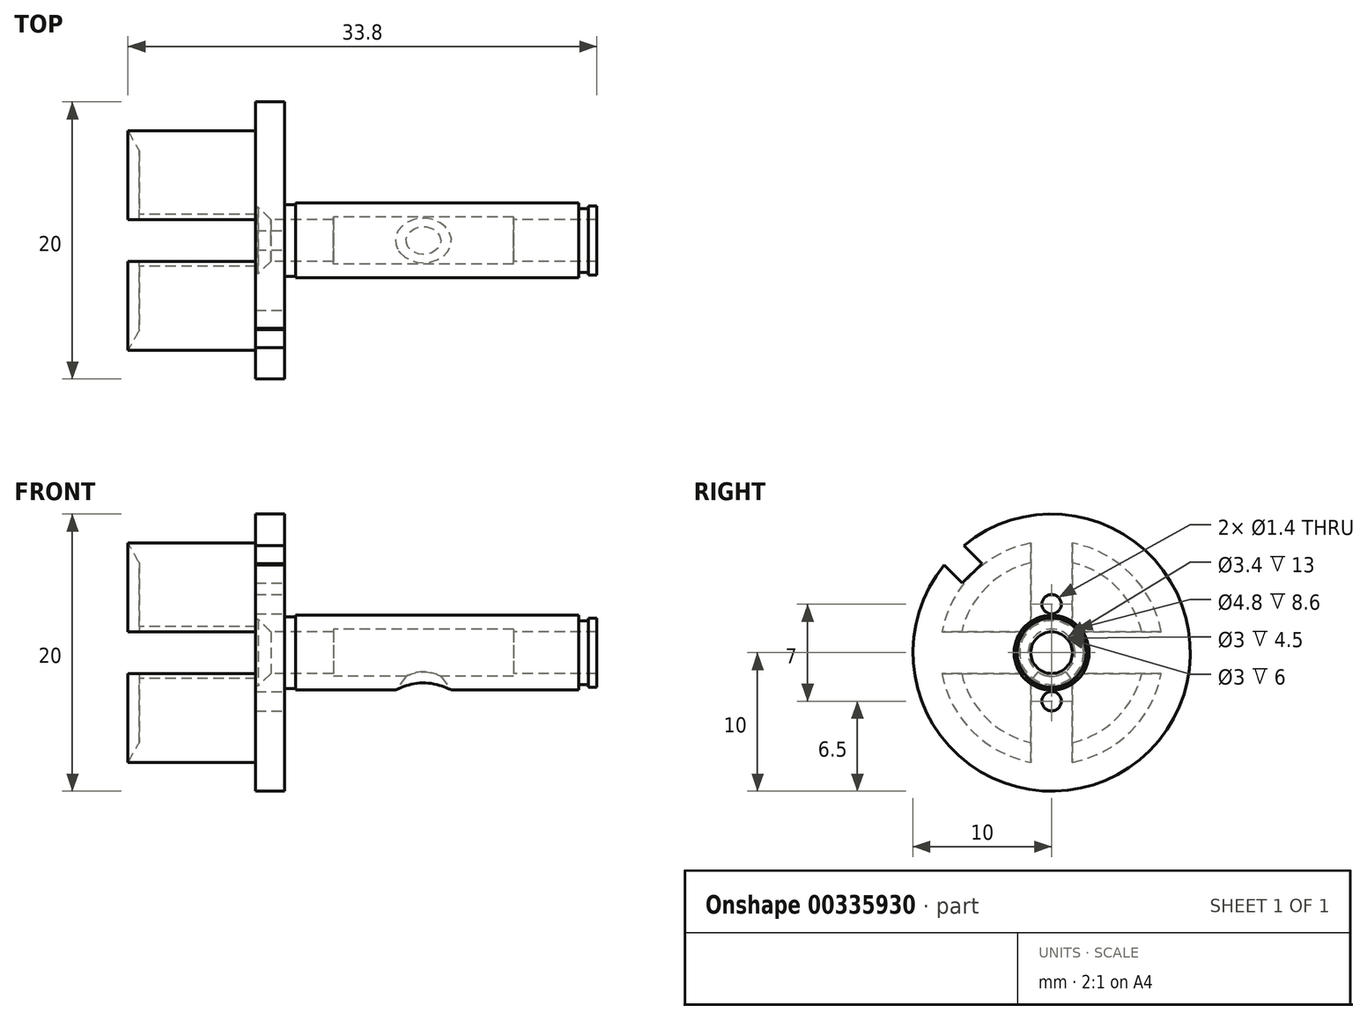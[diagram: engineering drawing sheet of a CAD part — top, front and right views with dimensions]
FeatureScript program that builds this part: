
annotation { "Feature Type Name" : "Feature", "Feature Type Description" : "" }
export const myFeature = defineFeature(function(context is Context, id is Id, definition is map)
    precondition{}
    {
        {
            var Q0;
            Q0=qCreatedBy(makeId("Front.planeOp"),FACE);
            var sketch = newSketch(context, id + "F0", { "sketchPlane" : qUnion([Q0])});
            skLineSegment(sketch, "E0", {"start": v(0, 8.05) * mm, "end": v(9.2, 8.05) * mm});
            skLineSegment(sketch, "E1", {"start": v(9.2, 8.05) * mm, "end": v(9.2, 10) * mm});
            skLineSegment(sketch, "E2", {"start": v(9.2, 10) * mm, "end": v(11.3, 10) * mm});
            skLineSegment(sketch, "E3", {"start": v(11.3, 10) * mm, "end": v(11.3, 2.6) * mm});
            skLineSegment(sketch, "E4", {"start": v(11.3, 2.6) * mm, "end": v(12.1, 2.6) * mm});
            skLineSegment(sketch, "E5", {"start": v(12.1, 2.6) * mm, "end": v(12.1, 2.7) * mm});
            skLineSegment(sketch, "E6", {"start": v(12.1, 2.7) * mm, "end": v(32.5, 2.7) * mm});
            skLineSegment(sketch, "E7", {"start": v(32.5, 2.7) * mm, "end": v(32.5, 2.3) * mm});
            skLineSegment(sketch, "E8", {"start": v(32.5, 2.3) * mm, "end": v(33.2, 2.3) * mm});
            skLineSegment(sketch, "E9", {"start": v(33.2, 2.3) * mm, "end": v(33.2, 2.5) * mm});
            skLineSegment(sketch, "E10", {"start": v(33.2, 2.5) * mm, "end": v(33.8, 2.5) * mm});
            skLineSegment(sketch, "E11", {"start": v(33.8, 2.5) * mm, "end": v(33.8, 1.5) * mm});
            skLineSegment(sketch, "E12", {"start": v(33.8, 1.5) * mm, "end": v(27.8, 1.5) * mm});
            skLineSegment(sketch, "E13", {"start": v(27.8, 1.5) * mm, "end": v(27.8, 1.7) * mm});
            skLineSegment(sketch, "E14", {"start": v(27.8, 1.7) * mm, "end": v(14.8, 1.7) * mm});
            skLineSegment(sketch, "E15", {"start": v(14.8, 1.7) * mm, "end": v(14.8, 1.5) * mm});
            skLineSegment(sketch, "E16", {"start": v(14.8, 1.5) * mm, "end": v(10.3, 1.5) * mm});
            skLineSegment(sketch, "E17", {"start": v(10.3, 1.5) * mm, "end": v(9.4, 2.4) * mm});
            skLineSegment(sketch, "E18", {"start": v(9.4, 2.4) * mm, "end": v(0.8, 2.4) * mm});
            skLineSegment(sketch, "E19", {"start": v(0.8, 2.4) * mm, "end": v(0.8, 6.66) * mm});
            skLineSegment(sketch, "E20", {"start": v(0.8, 6.66) * mm, "end": v(0, 8.05) * mm});
            skLineSegment(sketch, "E21", {"start": v(-0.32, 0) * mm, "end": v(33.8, 0) * mm});
            skLineSegment(sketch, "E22", {"start": v(17.46, -5.07) * mm, "end": v(21.3, -0.07) * mm});
            skLineSegment(sketch, "E23", {"start": v(21.3, -0.07) * mm, "end": v(25.14, -5.07) * mm});
            skLineSegment(sketch, "E24", {"start": v(20.05, -1.7) * mm, "end": v(22.55, -1.7) * mm, "construction": true});
            skLineSegment(sketch, "E25", {"start": v(21.3, -0.07) * mm, "end": v(21.3, -5.07) * mm});
            skLineSegment(sketch, "E26", {"start": v(17.46, -5.07) * mm, "end": v(25.14, -5.07) * mm});
            skSolve(sketch);
        }
        {
            var Q0;
            Q0=makeQuery(id+"F0.imprint","IMPRINT",FACE,{"disambiguationData":[TD([[makeQuery(id+"F0.imprint","IMPRINT",EDGE,{"derivedFrom":sQuery(id+"F0.wireOp",EDGE,"E0")}),-1.0]])]});
            var Q1;
            Q1=sQuery(id+"F0.wireOp",EDGE,"E21");
            revolve(context, id + "F1", {"entities" : qUnion([Q0]), "axis" : qUnion([Q1]), "revolveType" : RevolveType.FULL});
        }
        {
            var Q0;
            Q0=makeQuery(id+"F1.opRevolve","SWEPT_FACE",FACE,{"disambiguationData":[OSD([sQuery(id+"F0.wireOp",EDGE,"E1")])]});
            var sketch = newSketch(context, id + "F2", { "sketchPlane" : qUnion([Q0])});
            skCircle(sketch, "E27.0", {"center": v(0, 0) * mm, "radius": 10 * mm});
            skLineSegment(sketch, "E28", {"start": v(-1.5, 9.89) * mm, "end": v(-1.5, -9.89) * mm});
            skLineSegment(sketch, "E29", {"start": v(1.5, 9.89) * mm, "end": v(1.5, -9.89) * mm});
            skLineSegment(sketch, "E30", {"start": v(9.89, 1.5) * mm, "end": v(-9.89, 1.5) * mm});
            skLineSegment(sketch, "E31", {"start": v(-9.89, -1.5) * mm, "end": v(9.89, -1.5) * mm});
            skSolve(sketch);
        }
        {
            var Q0;
            {var subQ0=sQuery(id+"F2.wireOp",EDGE,"E30");var subQ1=sQuery(id+"F2.wireOp",EDGE,"E28");var subQ2=makeQuery(id+"F2.imprint","INTERSECT",VERTEX,{"derivedFrom":[subQ1,subQ0]});Q0=makeQuery(id+"F2.imprint","IMPRINT",FACE,{"disambiguationData":[TD([[makeQuery(id+"F2.imprint","IMPRINT",EDGE,{"disambiguationData":[TD([[subQ2,1.0]])],"derivedFrom":subQ0}),-1.0]])]});}
            var Q1;
            {var subQ0=sQuery(id+"F2.wireOp",EDGE,"E28");var subQ1=sQuery(id+"F2.wireOp",EDGE,"E27.0");var subQ2=makeQuery(id+"F2.imprint","INTERSECT",VERTEX,{"disambiguationData":[OD(0.0)],"derivedFrom":[subQ1,subQ0]});Q1=makeQuery(id+"F2.imprint","IMPRINT",FACE,{"disambiguationData":[TD([[makeQuery(id+"F2.imprint","IMPRINT",EDGE,{"disambiguationData":[TD([[subQ2,1.0]])],"derivedFrom":subQ1}),1.0]])]});}
            var Q2;
            {var subQ0=sQuery(id+"F2.wireOp",EDGE,"E30");var subQ1=sQuery(id+"F2.wireOp",EDGE,"E28");var subQ2=makeQuery(id+"F2.imprint","INTERSECT",VERTEX,{"derivedFrom":[subQ1,subQ0]});Q2=makeQuery(id+"F2.imprint","IMPRINT",FACE,{"disambiguationData":[TD([[makeQuery(id+"F2.imprint","IMPRINT",EDGE,{"disambiguationData":[TD([[subQ2,-1.0]])],"derivedFrom":subQ1}),-1.0]])]});}
            var Q3;
            {var subQ0=sQuery(id+"F2.wireOp",EDGE,"E30");var subQ1=sQuery(id+"F2.wireOp",EDGE,"E27.0");var subQ2=makeQuery(id+"F2.imprint","INTERSECT",VERTEX,{"disambiguationData":[OD(1.0)],"derivedFrom":[subQ1,subQ0]});Q3=makeQuery(id+"F2.imprint","IMPRINT",FACE,{"disambiguationData":[TD([[makeQuery(id+"F2.imprint","IMPRINT",EDGE,{"disambiguationData":[TD([[subQ2,-1.0]])],"derivedFrom":subQ1}),1.0]])]});}
            var Q4;
            {var subQ0=sQuery(id+"F2.wireOp",EDGE,"E30");var subQ1=sQuery(id+"F2.wireOp",EDGE,"E28");var subQ2=makeQuery(id+"F2.imprint","INTERSECT",VERTEX,{"derivedFrom":[subQ1,subQ0]});Q4=makeQuery(id+"F2.imprint","IMPRINT",FACE,{"disambiguationData":[TD([[makeQuery(id+"F2.imprint","IMPRINT",EDGE,{"disambiguationData":[TD([[subQ2,-1.0]])],"derivedFrom":subQ1}),1.0]])]});}
            var Q5;
            {var subQ0=sQuery(id+"F2.wireOp",EDGE,"E30");var subQ1=sQuery(id+"F2.wireOp",EDGE,"E29");var subQ2=makeQuery(id+"F2.imprint","INTERSECT",VERTEX,{"derivedFrom":[subQ1,subQ0]});Q5=makeQuery(id+"F2.imprint","IMPRINT",FACE,{"disambiguationData":[TD([[makeQuery(id+"F2.imprint","IMPRINT",EDGE,{"disambiguationData":[TD([[subQ2,-1.0]])],"derivedFrom":subQ1}),1.0]])]});}
            var Q6;
            {var subQ0=sQuery(id+"F2.wireOp",EDGE,"E30");var subQ1=sQuery(id+"F2.wireOp",EDGE,"E27.0");var subQ2=makeQuery(id+"F2.imprint","INTERSECT",VERTEX,{"disambiguationData":[OD(0.0)],"derivedFrom":[subQ1,subQ0]});Q6=makeQuery(id+"F2.imprint","IMPRINT",FACE,{"disambiguationData":[TD([[makeQuery(id+"F2.imprint","IMPRINT",EDGE,{"disambiguationData":[TD([[subQ2,1.0]])],"derivedFrom":subQ1}),1.0]])]});}
            var Q7;
            {var subQ0=sQuery(id+"F2.wireOp",EDGE,"E31");var subQ1=sQuery(id+"F2.wireOp",EDGE,"E28");var subQ2=makeQuery(id+"F2.imprint","INTERSECT",VERTEX,{"derivedFrom":[subQ1,subQ0]});Q7=makeQuery(id+"F2.imprint","IMPRINT",FACE,{"disambiguationData":[TD([[makeQuery(id+"F2.imprint","IMPRINT",EDGE,{"disambiguationData":[TD([[subQ2,-1.0]])],"derivedFrom":subQ0}),-1.0]])]});}
            var Q8;
            {var subQ0=sQuery(id+"F2.wireOp",EDGE,"E28");var subQ1=sQuery(id+"F2.wireOp",EDGE,"E27.0");var subQ2=makeQuery(id+"F2.imprint","INTERSECT",VERTEX,{"disambiguationData":[OD(1.0)],"derivedFrom":[subQ1,subQ0]});Q8=makeQuery(id+"F2.imprint","IMPRINT",FACE,{"disambiguationData":[TD([[makeQuery(id+"F2.imprint","IMPRINT",EDGE,{"disambiguationData":[TD([[subQ2,-1.0]])],"derivedFrom":subQ1}),1.0]])]});}
            extrude(context, id + "F3", {"entities" : qUnion([Q0, Q1, Q2, Q3, Q4, Q5, Q6, Q7, Q8]), "operationType" : NewBodyOperationType.REMOVE, "endBound" : BoundingType.THROUGH_ALL, "depth" : 25 * mm});
        }
        {
            var Q0;
            Q0=makeQuery(id+"F1.opRevolve","SWEPT_FACE",FACE,{"disambiguationData":[OSD([sQuery(id+"F0.wireOp",EDGE,"E3")])]});
            var sketch = newSketch(context, id + "F4", { "sketchPlane" : qUnion([Q0])});
            skCircle(sketch, "E32.0", {"center": v(0, 0) * mm, "radius": 10 * mm});
            skLineSegment(sketch, "E33", {"start": v(0, 0) * mm, "end": v(-7.07, 7.07) * mm, "construction": true});
            skLineSegment(sketch, "E34", {"start": v(-7.74, 6.33) * mm, "end": v(-6.43, 5.02) * mm});
            skLineSegment(sketch, "E35", {"start": v(-6.43, 5.02) * mm, "end": v(-5.02, 6.43) * mm});
            skLineSegment(sketch, "E36", {"start": v(-5.02, 6.43) * mm, "end": v(-6.33, 7.74) * mm});
            skPoint(sketch, "E37", {"position": v(-5.73, 5.73) * mm});
            skCircle(sketch, "E38", {"center": v(0, 0) * mm, "radius": 3.5 * mm, "construction": true});
            skCircle(sketch, "E39", {"center": v(0, 3.5) * mm, "radius": 0.7 * mm});
            skCircle(sketch, "E40", {"center": v(0, -3.5) * mm, "radius": 0.7 * mm});
            skSolve(sketch);
        }
        {
            var Q0;
            {var subQ0=sQuery(id+"F4.wireOp",EDGE,"E34");Q0=makeQuery(id+"F4.imprint","IMPRINT",FACE,{"disambiguationData":[TD([[makeQuery(id+"F4.imprint","IMPRINT",EDGE,{"derivedFrom":subQ0}),1.0]])]});}
            var Q1;
            Q1=makeQuery(id+"F4.imprint","IMPRINT",FACE,{"disambiguationData":[TD([[makeQuery(id+"F4.imprint","IMPRINT",EDGE,{"derivedFrom":sQuery(id+"F4.wireOp",EDGE,"E39")}),1.0]])]});
            var Q2;
            Q2=makeQuery(id+"F4.imprint","IMPRINT",FACE,{"disambiguationData":[TD([[makeQuery(id+"F4.imprint","IMPRINT",EDGE,{"derivedFrom":sQuery(id+"F4.wireOp",EDGE,"E40")}),1.0]])]});
            extrude(context, id + "F5", {"entities" : qUnion([Q0, Q1, Q2]), "operationType" : NewBodyOperationType.REMOVE, "endBound" : BoundingType.THROUGH_ALL, "oppositeDirection" : true, "depth" : 25 * mm});
        }
        {
            var Q0;
            {var subQ0=sQuery(id+"F0.wireOp",EDGE,"E23");Q0=makeQuery(id+"F0.imprint","IMPRINT",FACE,{"disambiguationData":[TD([[makeQuery(id+"F0.imprint","IMPRINT",EDGE,{"derivedFrom":subQ0}),-1.0]])]});}
            var Q1;
            Q1=sQuery(id+"F0.wireOp",EDGE,"E25");
            revolve(context, id + "F6", {"operationType" : NewBodyOperationType.REMOVE, "entities" : qUnion([Q0]), "axis" : qUnion([Q1]), "revolveType" : RevolveType.FULL, "oppositeDirection" : true});
        }
    });
